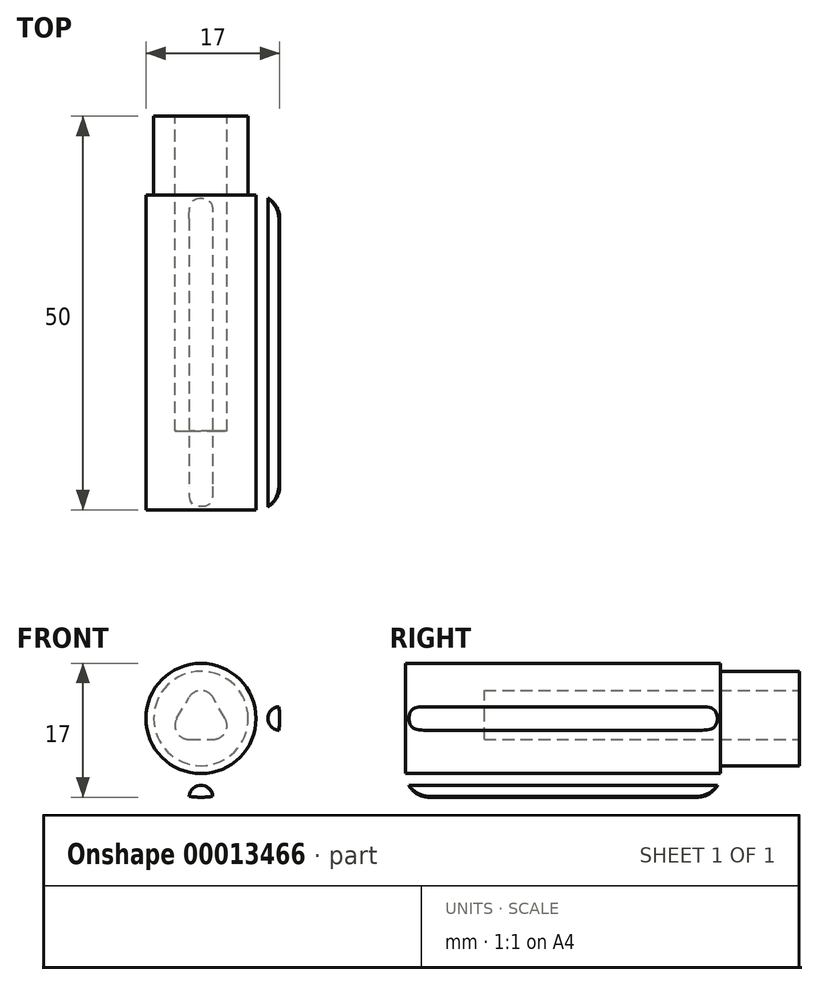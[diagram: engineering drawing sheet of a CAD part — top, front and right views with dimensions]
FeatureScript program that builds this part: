
annotation { "Feature Type Name" : "Feature", "Feature Type Description" : "" }
export const myFeature = defineFeature(function(context is Context, id is Id, definition is map)
    precondition{}
    {
        {
            var Q0;
            Q0=qCreatedBy(makeId("Front.planeOp"),FACE);
            var sketch = newSketch(context, id + "F0", { "sketchPlane" : qUnion([Q0])});
            skLineSegment(sketch, "E0", {"start": v(-1.55, -2.05) * mm, "end": v(1.55, -2.05) * mm});
            skArc(sketch, "E1", {"start": v(-1.55, -2.05) * mm, "mid": v(-2.55, -1.47) * mm, "end": v(-2.55, -0.32) * mm});
            skArc(sketch, "E2", {"start": v(1.55, -2.05) * mm, "mid": v(2.55, -1.47) * mm, "end": v(2.55, -0.32) * mm});
            skLineSegment(sketch, "E3", {"start": v(-2.55, -0.32) * mm, "end": v(-1, 2.37) * mm});
            skLineSegment(sketch, "E4", {"start": v(2.55, -0.32) * mm, "end": v(1, 2.37) * mm});
            skArc(sketch, "E5", {"start": v(1, 2.37) * mm, "mid": v(0, 2.95) * mm, "end": v(-1, 2.37) * mm});
            skCircle(sketch, "E6", {"center": v(0, 0) * mm, "radius": 1.8 * mm, "construction": true});
            skCircle(sketch, "E7", {"center": v(0, 0) * mm, "radius": 10 * mm});
            skLineSegment(sketch, "E8.0", {"start": v(-3.07, -0.02) * mm, "end": v(-1.52, 2.67) * mm});
            skArc(sketch, "E8.1", {"start": v(-1.55, -2.65) * mm, "mid": v(-3.07, -1.77) * mm, "end": v(-3.07, -0.02) * mm});
            skLineSegment(sketch, "E8.2", {"start": v(-1.55, -2.65) * mm, "end": v(1.55, -2.65) * mm});
            skArc(sketch, "E8.3", {"start": v(1.55, -2.65) * mm, "mid": v(3.07, -1.77) * mm, "end": v(3.07, -0.02) * mm});
            skLineSegment(sketch, "E8.4", {"start": v(3.07, -0.02) * mm, "end": v(1.52, 2.67) * mm});
            skArc(sketch, "E8.5", {"start": v(1.52, 2.67) * mm, "mid": v(0, 3.55) * mm, "end": v(-1.52, 2.67) * mm});
            skCircle(sketch, "E9", {"center": v(0, 0) * mm, "radius": 6 * mm});
            skSolve(sketch);
        }
        {
            var Q0;
            Q0=makeQuery(id+"F0.imprint","IMPRINT",FACE,{"disambiguationData":[TD([[makeQuery(id+"F0.imprint","IMPRINT",EDGE,{"derivedFrom":sQuery(id+"F0.wireOp",EDGE,"E7")}),1.0]])]});
            var Q1;
            Q1=makeQuery(id+"F0.imprint","IMPRINT",FACE,{"disambiguationData":[TD([[makeQuery(id+"F0.imprint","IMPRINT",EDGE,{"derivedFrom":sQuery(id+"F0.wireOp",EDGE,"E8.0")}),1.0]])]});
            var Q2;
            Q2=makeQuery(id+"F0.imprint","IMPRINT",FACE,{"disambiguationData":[TD([[makeQuery(id+"F0.imprint","IMPRINT",EDGE,{"derivedFrom":sQuery(id+"F0.wireOp",EDGE,"E0")}),-1.0]])]});
            var Q3;
            Q3=makeQuery(id+"F0.imprint","IMPRINT",FACE,{"disambiguationData":[TD([[makeQuery(id+"F0.imprint","IMPRINT",EDGE,{"derivedFrom":sQuery(id+"F0.wireOp",EDGE,"E0")}),1.0]])]});
            extrude(context, id + "F1", {"entities" : qUnion([Q0, Q1, Q2, Q3]), "depth" : 40 * mm});
        }
        {
            var Q0;
            Q0=makeQuery(id+"F0.imprint","IMPRINT",FACE,{"disambiguationData":[TD([[makeQuery(id+"F0.imprint","IMPRINT",EDGE,{"derivedFrom":sQuery(id+"F0.wireOp",EDGE,"E0")}),-1.0]])]});
            var Q1;
            Q1=makeQuery(id+"F0.imprint","IMPRINT",FACE,{"disambiguationData":[TD([[makeQuery(id+"F0.imprint","IMPRINT",EDGE,{"derivedFrom":sQuery(id+"F0.wireOp",EDGE,"E0")}),1.0]])]});
            extrude(context, id + "F2", {"entities" : qUnion([Q0, Q1]), "operationType" : NewBodyOperationType.REMOVE, "depth" : 30 * mm});
        }
        {
            var Q0;
            Q0=makeQuery(id+"F1.opExtrude","CAP_EDGE",EDGE,{"disambiguationData":[OSD([sQuery(id+"F0.wireOp",EDGE,"E7")])],"isStart":false});
            var Q1;
            Q1=makeQuery(id+"F1.opExtrude","CAP_EDGE",EDGE,{"disambiguationData":[OSD([sQuery(id+"F0.wireOp",EDGE,"E7")])],"isStart":true});
            fillet(context, id + "F3", {"entities" : qUnion([Q0, Q1]), "radius" : 3 * mm, "tangentPropagation" : true, "allowEdgeOverflow" : false});
        }
        {
            var Q0;
            Q0=makeQuery(id+"F1.opExtrude","CAP_FACE",FACE,{"disambiguationData":[OSD([sQuery(id+"F0.wireOp",EDGE,"E7")])],"isStart":false});
            var sketch = newSketch(context, id + "F4", { "sketchPlane" : qUnion([Q0])});
            skCircle(sketch, "E10.0", {"center": v(0, 0) * mm, "radius": 10 * mm});
            skCircle(sketch, "E11", {"center": v(-10, 0) * mm, "radius": 1.5 * mm});
            skCircle(sketch, "E12.1.0", {"center": v(-7.07, -7.07) * mm, "radius": 1.5 * mm});
            skCircle(sketch, "E12.2.0", {"center": v(0, -10) * mm, "radius": 1.5 * mm});
            skCircle(sketch, "E12.3.0", {"center": v(7.07, -7.07) * mm, "radius": 1.5 * mm});
            skCircle(sketch, "E12.4.0", {"center": v(10, 0) * mm, "radius": 1.5 * mm});
            skCircle(sketch, "E12.5.0", {"center": v(7.07, 7.07) * mm, "radius": 1.5 * mm});
            skCircle(sketch, "E12.6.0", {"center": v(0, 10) * mm, "radius": 1.5 * mm});
            skCircle(sketch, "E12.7.0", {"center": v(-7.07, 7.07) * mm, "radius": 1.5 * mm});
            skSolve(sketch);
        }
        {
            var Q0;
            {var subQ0=sQuery(id+"F4.wireOp",EDGE,"E11");var subQ1=sQuery(id+"F4.wireOp",EDGE,"E10.0");var subQ3=makeQuery(id+"F4.imprint","INTERSECT",VERTEX,{"disambiguationData":[OD(0.0)],"derivedFrom":[subQ1,subQ0]});Q0=makeQuery(id+"F4.imprint","IMPRINT",FACE,{"disambiguationData":[TD([[makeQuery(id+"F4.imprint","IMPRINT",EDGE,{"disambiguationData":[TD([[subQ3,-1.0]])],"derivedFrom":subQ1}),1.0]])]});}
            var Q1;
            {var subQ0=sQuery(id+"F4.wireOp",EDGE,"E12.1.0");var subQ1=sQuery(id+"F4.wireOp",EDGE,"E10.0");var subQ3=makeQuery(id+"F4.imprint","INTERSECT",VERTEX,{"disambiguationData":[OD(0.0)],"derivedFrom":[subQ1,subQ0]});Q1=makeQuery(id+"F4.imprint","IMPRINT",FACE,{"disambiguationData":[TD([[makeQuery(id+"F4.imprint","IMPRINT",EDGE,{"disambiguationData":[TD([[subQ3,-1.0]])],"derivedFrom":subQ1}),1.0]])]});}
            var Q2;
            {var subQ0=sQuery(id+"F4.wireOp",EDGE,"E12.2.0");var subQ1=sQuery(id+"F4.wireOp",EDGE,"E10.0");var subQ3=makeQuery(id+"F4.imprint","INTERSECT",VERTEX,{"disambiguationData":[OD(0.0)],"derivedFrom":[subQ1,subQ0]});Q2=makeQuery(id+"F4.imprint","IMPRINT",FACE,{"disambiguationData":[TD([[makeQuery(id+"F4.imprint","IMPRINT",EDGE,{"disambiguationData":[TD([[subQ3,-1.0]])],"derivedFrom":subQ1}),1.0]])]});}
            var Q3;
            {var subQ0=sQuery(id+"F4.wireOp",EDGE,"E12.3.0");var subQ1=sQuery(id+"F4.wireOp",EDGE,"E10.0");var subQ3=makeQuery(id+"F4.imprint","INTERSECT",VERTEX,{"disambiguationData":[OD(0.0)],"derivedFrom":[subQ1,subQ0]});Q3=makeQuery(id+"F4.imprint","IMPRINT",FACE,{"disambiguationData":[TD([[makeQuery(id+"F4.imprint","IMPRINT",EDGE,{"disambiguationData":[TD([[subQ3,-1.0]])],"derivedFrom":subQ1}),1.0]])]});}
            var Q4;
            {var subQ0=sQuery(id+"F4.wireOp",EDGE,"E12.4.0");var subQ1=sQuery(id+"F4.wireOp",EDGE,"E10.0");var subQ3=makeQuery(id+"F4.imprint","INTERSECT",VERTEX,{"disambiguationData":[OD(0.0)],"derivedFrom":[subQ1,subQ0]});Q4=makeQuery(id+"F4.imprint","IMPRINT",FACE,{"disambiguationData":[TD([[makeQuery(id+"F4.imprint","IMPRINT",EDGE,{"disambiguationData":[TD([[subQ3,1.0]])],"derivedFrom":subQ1}),1.0]])]});}
            var Q5;
            {var subQ0=sQuery(id+"F4.wireOp",EDGE,"E12.7.0");var subQ1=sQuery(id+"F4.wireOp",EDGE,"E10.0");var subQ3=makeQuery(id+"F4.imprint","INTERSECT",VERTEX,{"disambiguationData":[OD(0.0)],"derivedFrom":[subQ1,subQ0]});Q5=makeQuery(id+"F4.imprint","IMPRINT",FACE,{"disambiguationData":[TD([[makeQuery(id+"F4.imprint","IMPRINT",EDGE,{"disambiguationData":[TD([[subQ3,-1.0]])],"derivedFrom":subQ1}),1.0]])]});}
            var Q6;
            {var subQ0=sQuery(id+"F4.wireOp",EDGE,"E12.6.0");var subQ1=sQuery(id+"F4.wireOp",EDGE,"E10.0");var subQ3=makeQuery(id+"F4.imprint","INTERSECT",VERTEX,{"disambiguationData":[OD(0.0)],"derivedFrom":[subQ1,subQ0]});Q6=makeQuery(id+"F4.imprint","IMPRINT",FACE,{"disambiguationData":[TD([[makeQuery(id+"F4.imprint","IMPRINT",EDGE,{"disambiguationData":[TD([[subQ3,-1.0]])],"derivedFrom":subQ1}),1.0]])]});}
            var Q7;
            {var subQ0=sQuery(id+"F4.wireOp",EDGE,"E12.5.0");var subQ1=sQuery(id+"F4.wireOp",EDGE,"E10.0");var subQ3=makeQuery(id+"F4.imprint","INTERSECT",VERTEX,{"disambiguationData":[OD(0.0)],"derivedFrom":[subQ1,subQ0]});Q7=makeQuery(id+"F4.imprint","IMPRINT",FACE,{"disambiguationData":[TD([[makeQuery(id+"F4.imprint","IMPRINT",EDGE,{"disambiguationData":[TD([[subQ3,-1.0]])],"derivedFrom":subQ1}),1.0]])]});}
            extrude(context, id + "F5", {"entities" : qUnion([Q0, Q1, Q2, Q3, Q4, Q5, Q6, Q7]), "operationType" : NewBodyOperationType.REMOVE, "endBound" : BoundingType.THROUGH_ALL, "oppositeDirection" : true, "depth" : 25 * mm});
        }
        {
            var Q0;
            Q0=makeQuery(id+"F0.imprint","IMPRINT",FACE,{"disambiguationData":[TD([[makeQuery(id+"F0.imprint","IMPRINT",EDGE,{"derivedFrom":sQuery(id+"F0.wireOp",EDGE,"E8.0")}),1.0]])]});
            extrude(context, id + "F6", {"entities" : qUnion([Q0]), "operationType" : NewBodyOperationType.ADD, "oppositeDirection" : true, "depth" : 10 * mm});
        }
    });
